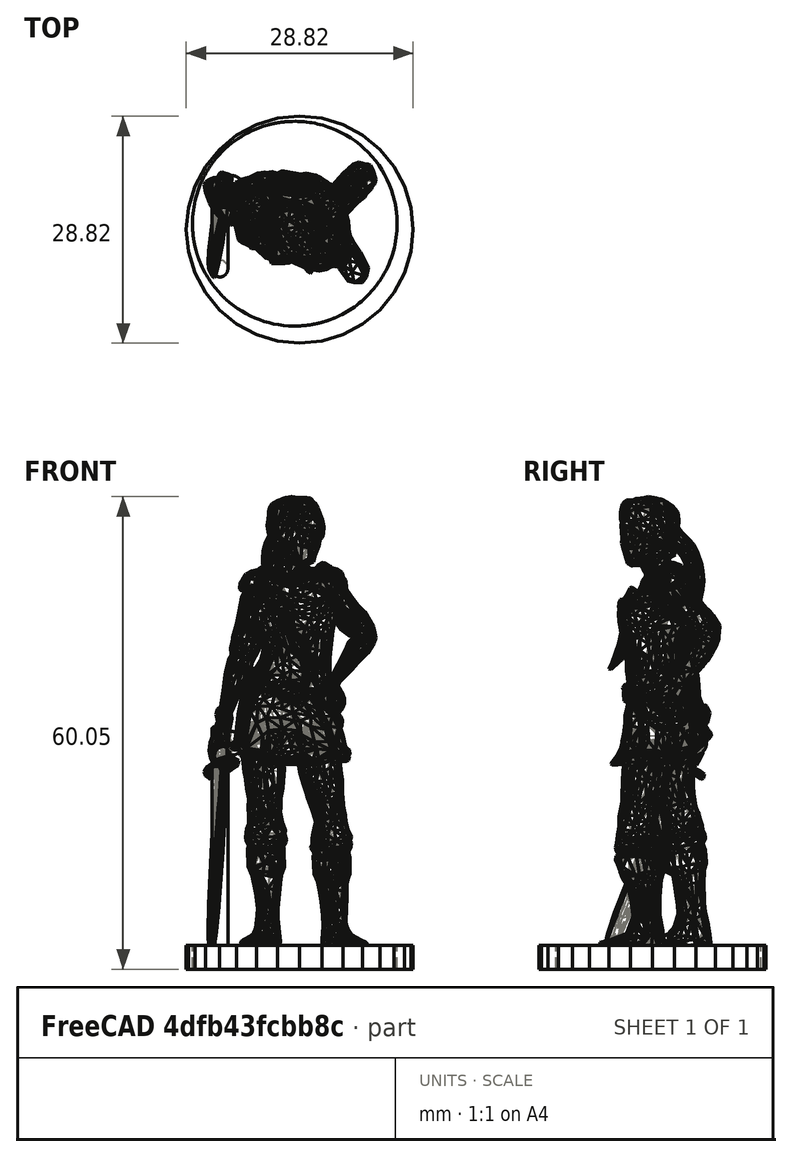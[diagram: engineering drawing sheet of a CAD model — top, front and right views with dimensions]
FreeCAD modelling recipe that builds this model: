
FCSTD DOCUMENT  (FreeCAD 0.17R13541 (Git))
Label: SR4fixNoBase
License: All rights reserved
LicenseURL: http://en.wikipedia.org/wiki/All_rights_reserved
objects: Part::Feature×3, Part::Cylinder×3, Part::Cut×2, Part::Fuse×2, Mesh::Feature×1, Part::Sphere×1
note: 11 computed .brp shape members not serialized (recipe doc carries the construction recipe); baked Part::Feature solids carry a one-line shape summary decoded from their .brp

FEATURE [Mesh::Feature] FemaleKnight_StandRelaxed_Cleaned4
FEATURE [Part::Feature] FemaleKnight_StandRelaxed_Cleaned4001
  shape: bbox 28.82 x 28.82 x 60.05 mm, 8000 faces, 0 solids (baked)
FEATURE [Part::Feature] FemaleKnight_StandRelaxed_Cleaned4001_solid  label="FemaleKnight_StandRelaxed_Cleaned4001 (Solid)"
  shape: bbox 28.82 x 28.82 x 60.05 mm, 8000 faces (baked)
FEATURE [Part::Cylinder] Cylinder001
  Angle = 360
  AttacherType = Attacher::AttachEngine3D
  Height = 7
  Radius = 13
FEATURE [Part::Cylinder] Cylinder002
  Angle = 360
  AttacherType = Attacher::AttachEngine3D
  Height = 7
  Radius = 16
FEATURE [Part::Cut] Cut
  Base = -> Cylinder002
  Tool = -> Cylinder001
FEATURE [Part::Cut] Cut001
  Base = -> FemaleKnight_StandRelaxed_Cleaned4001_solid
  Tool = -> Cut
FEATURE [Part::Feature] FemaleKnight_StandRelaxed_Cleaned4001_solid001  label="FemaleKnight_StandRelaxed_Cleaned4001 (Solid)001"
  shape: bbox 28.82 x 28.82 x 60.05 mm, 8000 faces (baked)
FEATURE [Part::Cylinder] Cylinder
  Angle = 360
  AttacherType = Attacher::AttachEngine3D
  Height = 32
  Placement = pos=(-9.5,-6.6,1) rot=(-1,0,0;0.366519rad)
  Radius = 1
FEATURE [Part::Sphere] Sphere
  Angle1 = -90
  Angle2 = 90
  Angle3 = 360
  AttacherType = Attacher::AttachEngine3D
  Placement = pos=(-8,4.6,29) rot=(0,0,1;0rad)
  Radius = 1.5
FEATURE [Part::Fuse] Fusion
  Base = -> FemaleKnight_StandRelaxed_Cleaned4001_solid001
  Tool = -> Cylinder
FEATURE [Part::Fuse] Fusion001
  Base = -> Fusion
  Tool = -> Sphere
